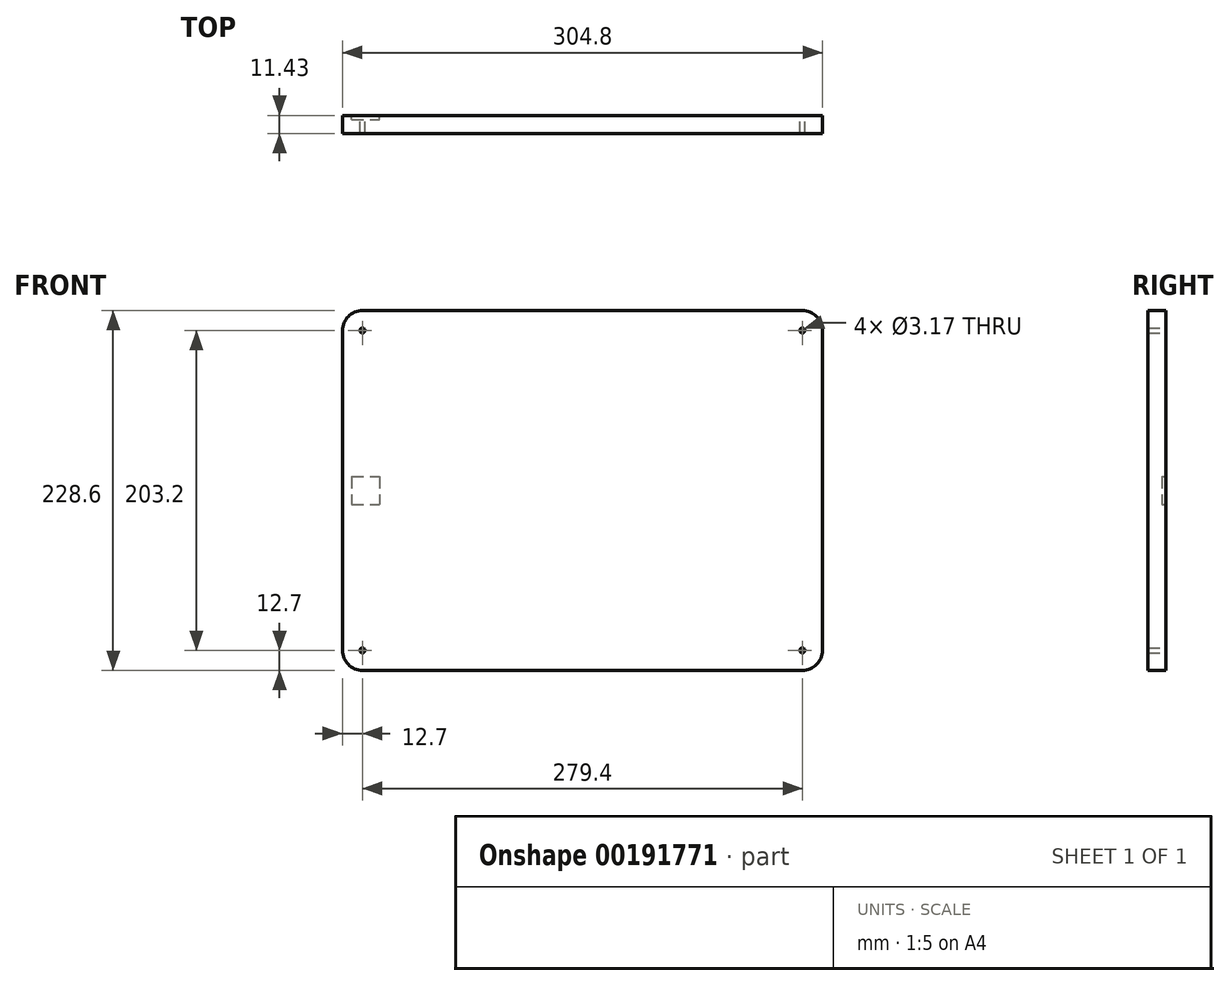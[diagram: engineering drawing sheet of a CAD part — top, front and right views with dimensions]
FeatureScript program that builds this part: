
annotation { "Feature Type Name" : "Feature", "Feature Type Description" : "" }
export const myFeature = defineFeature(function(context is Context, id is Id, definition is map)
    precondition{}
    {
        {
            var Q0;
            Q0=qCreatedBy(makeId("Front.planeOp"),FACE);
            var sketch = newSketch(context, id + "F0", { "sketchPlane" : qUnion([Q0])});
            skLineSegment(sketch, "E0.bottom", {"start": v(12.7, 228.6) * mm, "end": v(292.1, 228.6) * mm});
            skLineSegment(sketch, "E0.top", {"start": v(12.7, 0) * mm, "end": v(292.1, 0) * mm});
            skLineSegment(sketch, "E0.left", {"start": v(0, 215.9) * mm, "end": v(0, 12.7) * mm});
            skLineSegment(sketch, "E0.right", {"start": v(304.8, 215.9) * mm, "end": v(304.8, 12.7) * mm});
            skPoint(sketch, "E1.visualSharp", {"position": v(0, 228.6) * mm});
            skArc(sketch, "E1.filletArc", {"start": v(12.7, 228.6) * mm, "mid": v(3.72, 224.88) * mm, "end": v(0, 215.9) * mm});
            skPoint(sketch, "E2.visualSharp", {"position": v(304.8, 228.6) * mm});
            skArc(sketch, "E2.filletArc", {"start": v(304.8, 215.9) * mm, "mid": v(301.08, 224.88) * mm, "end": v(292.1, 228.6) * mm});
            skPoint(sketch, "E3.visualSharp", {"position": v(304.8, 0) * mm});
            skArc(sketch, "E3.filletArc", {"start": v(292.1, 0) * mm, "mid": v(301.08, 3.72) * mm, "end": v(304.8, 12.7) * mm});
            skPoint(sketch, "E4.visualSharp", {"position": v(0, 0) * mm});
            skArc(sketch, "E4.filletArc", {"start": v(0, 12.7) * mm, "mid": v(3.72, 3.72) * mm, "end": v(12.7, 0) * mm});
            skCircle(sketch, "E5", {"center": v(12.7, 215.9) * mm, "radius": 1.59 * mm});
            skCircle(sketch, "E6", {"center": v(292.1, 215.9) * mm, "radius": 1.59 * mm});
            skCircle(sketch, "E7", {"center": v(12.7, 12.7) * mm, "radius": 1.59 * mm});
            skCircle(sketch, "E8", {"center": v(292.1, 12.7) * mm, "radius": 1.59 * mm});
            skSolve(sketch);
        }
        {
            var Q0;
            Q0=makeQuery(id+"F0.imprint","IMPRINT",FACE,{"disambiguationData":[TD([[makeQuery(id+"F0.imprint","IMPRINT",EDGE,{"derivedFrom":sQuery(id+"F0.wireOp",EDGE,"E0.bottom")}),-1.0]])]});
            var sketch = newSketch(context, id + "F1", { "sketchPlane" : qUnion([Q0])});
            skLineSegment(sketch, "E9.0", {"start": v(5.9, 123.2) * mm, "end": v(23.67, 123.2) * mm});
            skLineSegment(sketch, "E9.1", {"start": v(5.9, 105.4) * mm, "end": v(23.67, 105.4) * mm});
            skLineSegment(sketch, "E9.2", {"start": v(23.67, 123.2) * mm, "end": v(23.67, 105.4) * mm});
            skLineSegment(sketch, "E9.3", {"start": v(5.9, 123.2) * mm, "end": v(5.9, 105.4) * mm});
            skSolve(sketch);
        }
        {
            var Q0;
            Q0 = qSketchRegion(id + "F0", true);
            extrude(context, id + "F2", {"entities" : qUnion([Q0]), "depth" : 11.43 * mm});
        }
        {
            var Q0;
            Q0 = qSketchRegion(id + "F1", true);
            extrude(context, id + "F3", {"entities" : qUnion([Q0]), "operationType" : NewBodyOperationType.REMOVE, "depth" : 2.54 * mm});
        }
    });
